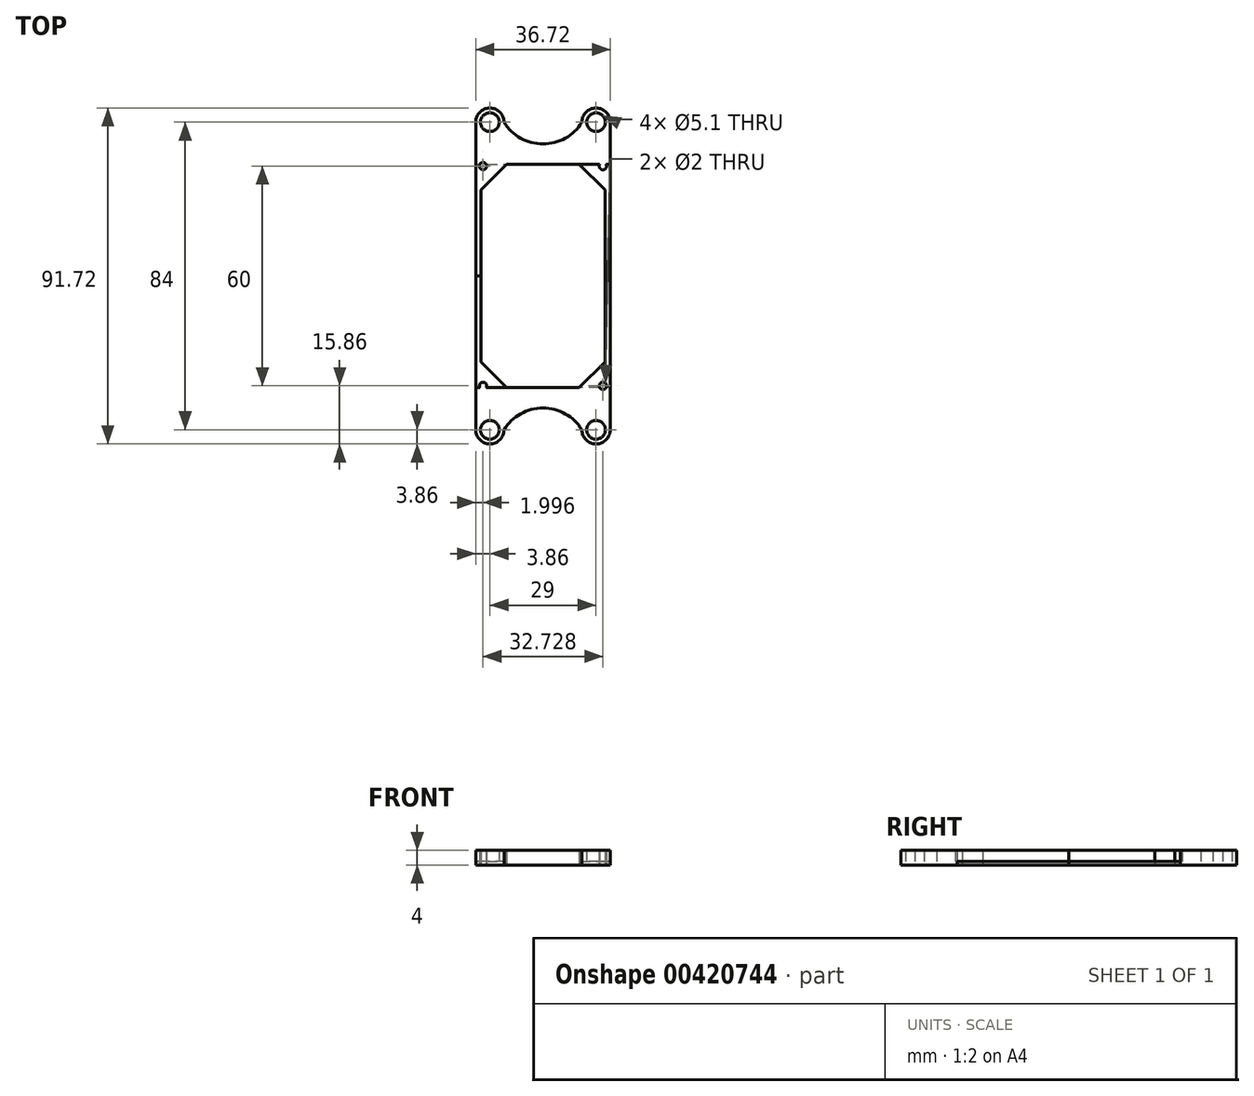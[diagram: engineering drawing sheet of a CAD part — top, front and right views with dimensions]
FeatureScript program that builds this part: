
annotation { "Feature Type Name" : "Feature", "Feature Type Description" : "" }
export const myFeature = defineFeature(function(context is Context, id is Id, definition is map)
    precondition{}
    {
        {
            var Q0;
            Q0=qCreatedBy(makeId("Top.planeOp"),FACE);
            var sketch = newSketch(context, id + "F0", { "sketchPlane" : qUnion([Q0])});
            skLineSegment(sketch, "E0.MirrorCS", {"start": v(9.93, 30.5) * mm, "end": v(16.93, 23.5) * mm});
            skLineSegment(sketch, "E1.MirrorCS", {"start": v(18.36, 30.5) * mm, "end": v(18.36, 0) * mm});
            skCircle(sketch, "E2.MirrorC", {"center": v(16.36, 30) * mm, "radius": 1 * mm});
            skLineSegment(sketch, "E3", {"start": v(16.93, 23.5) * mm, "end": v(16.93, 0) * mm});
            skLineSegment(sketch, "E4", {"start": v(16.93, 0) * mm, "end": v(18.36, 0) * mm});
            skLineSegment(sketch, "E5.MirrorCS", {"start": v(-18.36, 30.5) * mm, "end": v(-18.36, 0) * mm});
            skLineSegment(sketch, "E6.MirrorCS", {"start": v(-16.93, 23.5) * mm, "end": v(-16.93, 0) * mm});
            skLineSegment(sketch, "E7.MirrorCS", {"start": v(-9.93, 30.5) * mm, "end": v(-16.93, 23.5) * mm});
            skCircle(sketch, "E8.MirrorC", {"center": v(-16.36, 30) * mm, "radius": 1 * mm});
            skLineSegment(sketch, "E9.MirrorCS", {"start": v(-16.93, 0) * mm, "end": v(-18.36, 0) * mm});
            skCircle(sketch, "E10.MirrorC", {"center": v(-16.36, -30) * mm, "radius": 1 * mm});
            skCircle(sketch, "E11.MirrorC", {"center": v(16.36, -30) * mm, "radius": 1 * mm});
            skLineSegment(sketch, "E12.MirrorCS", {"start": v(-16.93, -23.5) * mm, "end": v(-16.93, 0) * mm});
            skLineSegment(sketch, "E13.MirrorCS", {"start": v(16.93, -23.5) * mm, "end": v(16.93, 0) * mm});
            skLineSegment(sketch, "E14.MirrorCS", {"start": v(18.36, -30.5) * mm, "end": v(18.36, 0) * mm});
            skLineSegment(sketch, "E15.MirrorCS", {"start": v(-18.36, -30.5) * mm, "end": v(-18.36, 0) * mm});
            skLineSegment(sketch, "E16.MirrorCS", {"start": v(9.93, -30.5) * mm, "end": v(16.93, -23.5) * mm});
            skLineSegment(sketch, "E17.MirrorCS", {"start": v(-9.93, -30.5) * mm, "end": v(-16.93, -23.5) * mm});
            skLineSegment(sketch, "E18", {"start": v(18.36, 30.5) * mm, "end": v(0, 30.5) * mm});
            skLineSegment(sketch, "E19", {"start": v(18.36, 42) * mm, "end": v(18.36, 0) * mm});
            skCircle(sketch, "E20", {"center": v(14.5, 42) * mm, "radius": 2.55 * mm});
            skArc(sketch, "E21", {"start": v(18.36, 42) * mm, "mid": v(14.5, 45.86) * mm, "end": v(10.64, 42) * mm});
            skPoint(sketch, "E22.orphan", {"position": v(18.36, 0) * mm});
            skLineSegment(sketch, "E23.MirrorCS", {"start": v(-18.36, 30.5) * mm, "end": v(0, 30.5) * mm});
            skArc(sketch, "E24.MirrorCS", {"start": v(-18.36, 42) * mm, "mid": v(-14.5, 45.86) * mm, "end": v(-10.64, 42) * mm});
            skCircle(sketch, "E25.MirrorC", {"center": v(-14.5, 42) * mm, "radius": 2.55 * mm});
            skLineSegment(sketch, "E26.MirrorCS", {"start": v(-18.36, 42) * mm, "end": v(-18.36, 0) * mm});
            skLineSegment(sketch, "E27.MirrorCS", {"start": v(-18.36, -30.5) * mm, "end": v(0, -30.5) * mm});
            skLineSegment(sketch, "E28.MirrorCS", {"start": v(-18.36, -42) * mm, "end": v(-18.36, 0) * mm});
            skCircle(sketch, "E29.MirrorC", {"center": v(-14.5, -42) * mm, "radius": 2.55 * mm});
            skArc(sketch, "E30.MirrorCS", {"start": v(-18.36, -42) * mm, "mid": v(-14.5, -45.86) * mm, "end": v(-10.64, -42) * mm});
            skArc(sketch, "E31.MirrorCS", {"start": v(18.36, -42) * mm, "mid": v(14.5, -45.86) * mm, "end": v(10.64, -42) * mm});
            skCircle(sketch, "E32.MirrorC", {"center": v(14.5, -42) * mm, "radius": 2.55 * mm});
            skLineSegment(sketch, "E33.MirrorCS", {"start": v(18.36, -30.5) * mm, "end": v(0, -30.5) * mm});
            skLineSegment(sketch, "E34.MirrorCS", {"start": v(18.36, -42) * mm, "end": v(18.36, 0) * mm});
            skArc(sketch, "E35", {"start": v(-10.64, 42) * mm, "mid": v(0, 36.05) * mm, "end": v(10.64, 42) * mm});
            skArc(sketch, "E36.MirrorCS", {"start": v(-10.64, -42) * mm, "mid": v(0, -36.05) * mm, "end": v(10.64, -42) * mm});
            skSolve(sketch);
        }
        {
            var Q0;
            {var subQ4=sQuery(id+"F0.wireOp",EDGE,"E6.MirrorCS");Q0=makeQuery(id+"F0.imprint","IMPRINT",FACE,{"disambiguationData":[TD([[makeQuery(id+"F0.imprint","IMPRINT",EDGE,{"derivedFrom":subQ4}),-1.0]])]});}
            var Q1;
            {var subQ0=sQuery(id+"F0.wireOp",EDGE,"E9.MirrorCS");Q1=makeQuery(id+"F0.imprint","IMPRINT",FACE,{"disambiguationData":[TD([[makeQuery(id+"F0.imprint","IMPRINT",EDGE,{"derivedFrom":subQ0}),1.0]])]});}
            var Q2;
            {var subQ3=sQuery(id+"F0.wireOp",EDGE,"E3");Q2=makeQuery(id+"F0.imprint","IMPRINT",FACE,{"disambiguationData":[TD([[makeQuery(id+"F0.imprint","IMPRINT",EDGE,{"derivedFrom":subQ3}),1.0]])]});}
            var Q3;
            {var subQ0=sQuery(id+"F0.wireOp",EDGE,"E4");Q3=makeQuery(id+"F0.imprint","IMPRINT",FACE,{"disambiguationData":[TD([[makeQuery(id+"F0.imprint","IMPRINT",EDGE,{"derivedFrom":subQ0}),-1.0]])]});}
            extrude(context, id + "F1", {"entities" : qUnion([Q0, Q1, Q2, Q3]), "depth" : 1 * mm, "offsetDistance" : 25 * mm});
        }
        {
            var Q0;
            Q0=makeQuery(id+"F0.imprint","IMPRINT",FACE,{"disambiguationData":[TD([[makeQuery(id+"F0.imprint","IMPRINT",EDGE,{"derivedFrom":sQuery(id+"F0.wireOp",EDGE,"E20")}),-1.0]])]});
            var Q1;
            Q1=makeQuery(id+"F0.imprint","IMPRINT",FACE,{"disambiguationData":[TD([[makeQuery(id+"F0.imprint","IMPRINT",EDGE,{"derivedFrom":sQuery(id+"F0.wireOp",EDGE,"E29.MirrorC")}),-1.0]])]});
            var Q2;
            Q2=makeQuery(id+"F0.imprint","IMPRINT",FACE,{"disambiguationData":[TD([[makeQuery(id+"F0.imprint","IMPRINT",EDGE,{"derivedFrom":sQuery(id+"F0.wireOp",EDGE,"E2.MirrorC")}),1.0]])]});
            var Q3;
            Q3=makeQuery(id+"F0.imprint","IMPRINT",FACE,{"disambiguationData":[TD([[makeQuery(id+"F0.imprint","IMPRINT",EDGE,{"derivedFrom":sQuery(id+"F0.wireOp",EDGE,"E8.MirrorC")}),-1.0]])]});
            var Q4;
            Q4=makeQuery(id+"F0.imprint","IMPRINT",FACE,{"disambiguationData":[TD([[makeQuery(id+"F0.imprint","IMPRINT",EDGE,{"derivedFrom":sQuery(id+"F0.wireOp",EDGE,"E11.MirrorC")}),-1.0]])]});
            var Q5;
            Q5=makeQuery(id+"F0.imprint","IMPRINT",FACE,{"disambiguationData":[TD([[makeQuery(id+"F0.imprint","IMPRINT",EDGE,{"derivedFrom":sQuery(id+"F0.wireOp",EDGE,"E10.MirrorC")}),1.0]])]});
            extrude(context, id + "F2", {"entities" : qUnion([Q0, Q1, Q2, Q3, Q4, Q5]), "depth" : 4 * mm, "offsetDistance" : 25 * mm});
        }
    });
